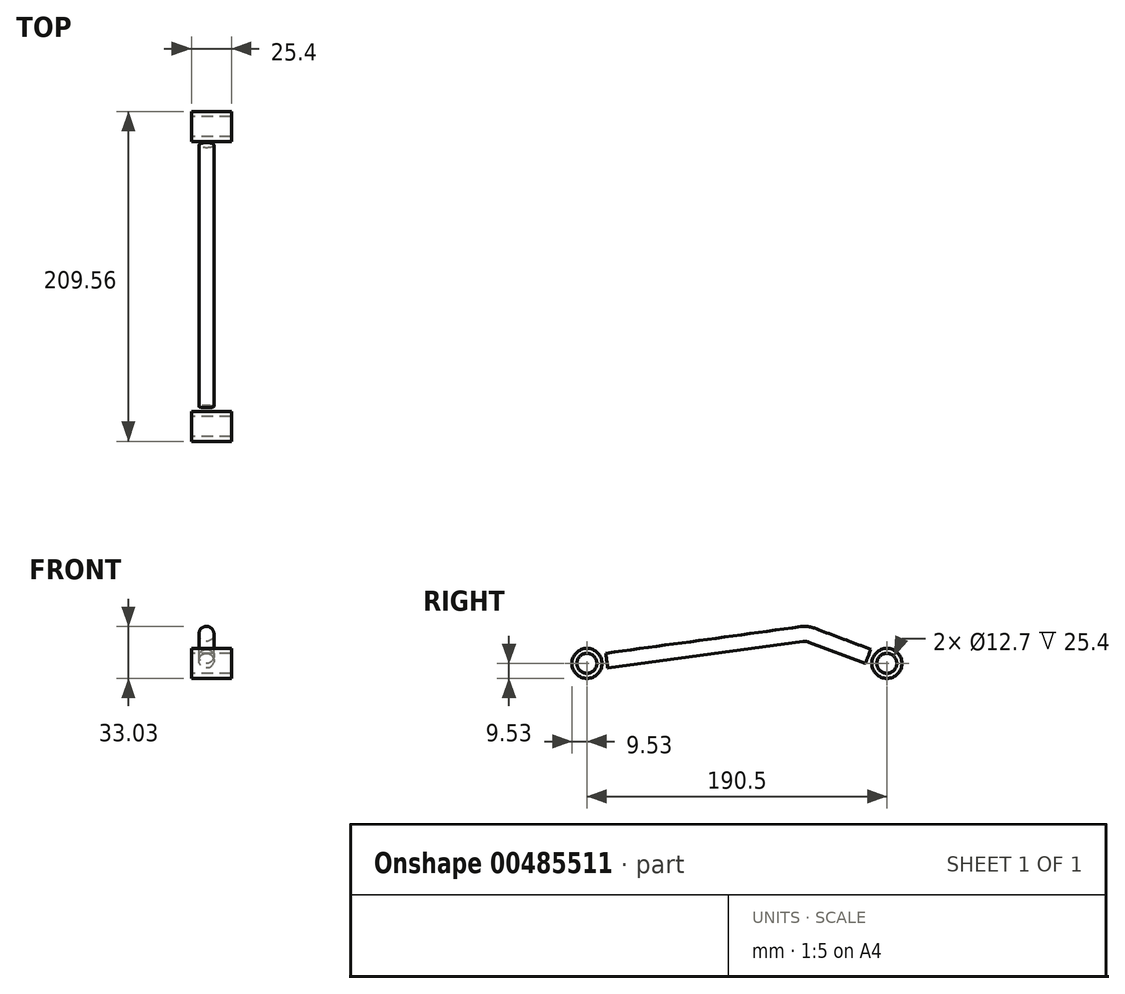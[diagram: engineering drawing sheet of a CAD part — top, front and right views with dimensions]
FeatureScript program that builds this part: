
annotation { "Feature Type Name" : "Feature", "Feature Type Description" : "" }
export const myFeature = defineFeature(function(context is Context, id is Id, definition is map)
    precondition{}
    {
        {
            var Q0;
            Q0=qCreatedBy(makeId("Right.planeOp"),FACE);
            var sketch = newSketch(context, id + "F0", { "sketchPlane" : qUnion([Q0])});
            skCircle(sketch, "E0", {"center": v(0, 0) * mm, "radius": 9.53 * mm});
            skCircle(sketch, "E1", {"center": v(190.5, 0) * mm, "radius": 9.53 * mm});
            skCircle(sketch, "E2", {"center": v(0, 0) * mm, "radius": 6.35 * mm});
            skCircle(sketch, "E3", {"center": v(190.5, 0) * mm, "radius": 6.35 * mm});
            skSolve(sketch);
        }
        {
            var Q0;
            Q0 = qSketchRegion(id + "F0", true);
            extrude(context, id + "F1", {"entities" : qUnion([Q0]), "depth" : 25.4 * mm});
        }
        {
            var Q0;
            Q0=qCreatedBy(makeId("Right.planeOp"),FACE);
            cPlane(context, id + "F2", {"entities" : qUnion([Q0]), "cplaneType" : CPlaneType.OFFSET, "offset" : 9.52 * mm, "width" : 152.4 * mm, "height" : 152.4 * mm});
        }
        {
            var Q0;
            Q0=qCreatedBy(id+"F2.planeOp",FACE);
            var sketch = newSketch(context, id + "F3", { "sketchPlane" : qUnion([Q0])});
            skPoint(sketch, "E4.visualSharp", {"position": v(139.7, 19.05) * mm});
            skCircle(sketch, "E5", {"center": v(0, 0) * mm, "radius": 12.7 * mm});
            skCircle(sketch, "E6", {"center": v(190.5, 0) * mm, "radius": 12.7 * mm});
            skLineSegment(sketch, "E7", {"start": v(11.94, 6.43) * mm, "end": v(13.23, -3) * mm});
            skLineSegment(sketch, "E8.0", {"start": v(141.03, 13.47) * mm, "end": v(177.8, -0.33) * mm});
            skArc(sketch, "E8.1", {"start": v(141.03, 13.47) * mm, "mid": v(139.13, 13.92) * mm, "end": v(137.17, 13.9) * mm});
            skLineSegment(sketch, "E8.2", {"start": v(13.23, -3) * mm, "end": v(137.17, 13.9) * mm});
            skLineSegment(sketch, "E9.0", {"start": v(144.37, 22.38) * mm, "end": v(181.15, 8.6) * mm});
            skArc(sketch, "E9.1", {"start": v(144.37, 22.38) * mm, "mid": v(140.19, 23.39) * mm, "end": v(135.88, 23.34) * mm});
            skLineSegment(sketch, "E9.2", {"start": v(11.94, 6.43) * mm, "end": v(135.88, 23.34) * mm});
            skLineSegment(sketch, "E10", {"start": v(180.28, 8.92) * mm, "end": v(176.94, 0) * mm});
            skPoint(sketch, "E11.orphan", {"position": v(166.65, -27.43) * mm});
            skPoint(sketch, "E12.orphan", {"position": v(190.57, 36.35) * mm});
            skPoint(sketch, "E13.start.orphan", {"position": v(12.58, 1.72) * mm});
            skPoint(sketch, "E14.end.orphan", {"position": v(178.6, 4.46) * mm});
            skSolve(sketch);
        }
        {
            var Q0;
            {var subQ0=sQuery(id+"F3.wireOp",EDGE,"E8.1");Q0=makeQuery(id+"F3.imprint","IMPRINT",FACE,{"disambiguationData":[TD([[makeQuery(id+"F3.imprint","IMPRINT",EDGE,{"derivedFrom":subQ0}),-1.0]])]});}
            extrude(context, id + "F4", {"entities" : qUnion([Q0]), "endBound" : BoundingType.SYMMETRIC, "depth" : 9.52 * mm});
        }
        {
            var Q0;
            Q0=makeQuery(id+"F4.opExtrude","CAP_EDGE",EDGE,{"disambiguationData":[OSD([sQuery(id+"F3.wireOp",EDGE,"E8.2")])],"isStart":false});
            var Q1;
            Q1=makeQuery(id+"F4.opExtrude","CAP_EDGE",EDGE,{"disambiguationData":[OSD([sQuery(id+"F3.wireOp",EDGE,"E9.2")])],"isStart":false});
            var Q2;
            Q2=makeQuery(id+"F4.opExtrude","CAP_EDGE",EDGE,{"disambiguationData":[OSD([sQuery(id+"F3.wireOp",EDGE,"E9.2")])],"isStart":true});
            var Q3;
            Q3=makeQuery(id+"F4.opExtrude","CAP_EDGE",EDGE,{"disambiguationData":[OSD([sQuery(id+"F3.wireOp",EDGE,"E8.2")])],"isStart":true});
            fillet(context, id + "F5", {"entities" : qUnion([Q0, Q1, Q2, Q3]), "radius" : 4.76 * mm, "tangentPropagation" : true, "allowEdgeOverflow" : false});
        }
    });
